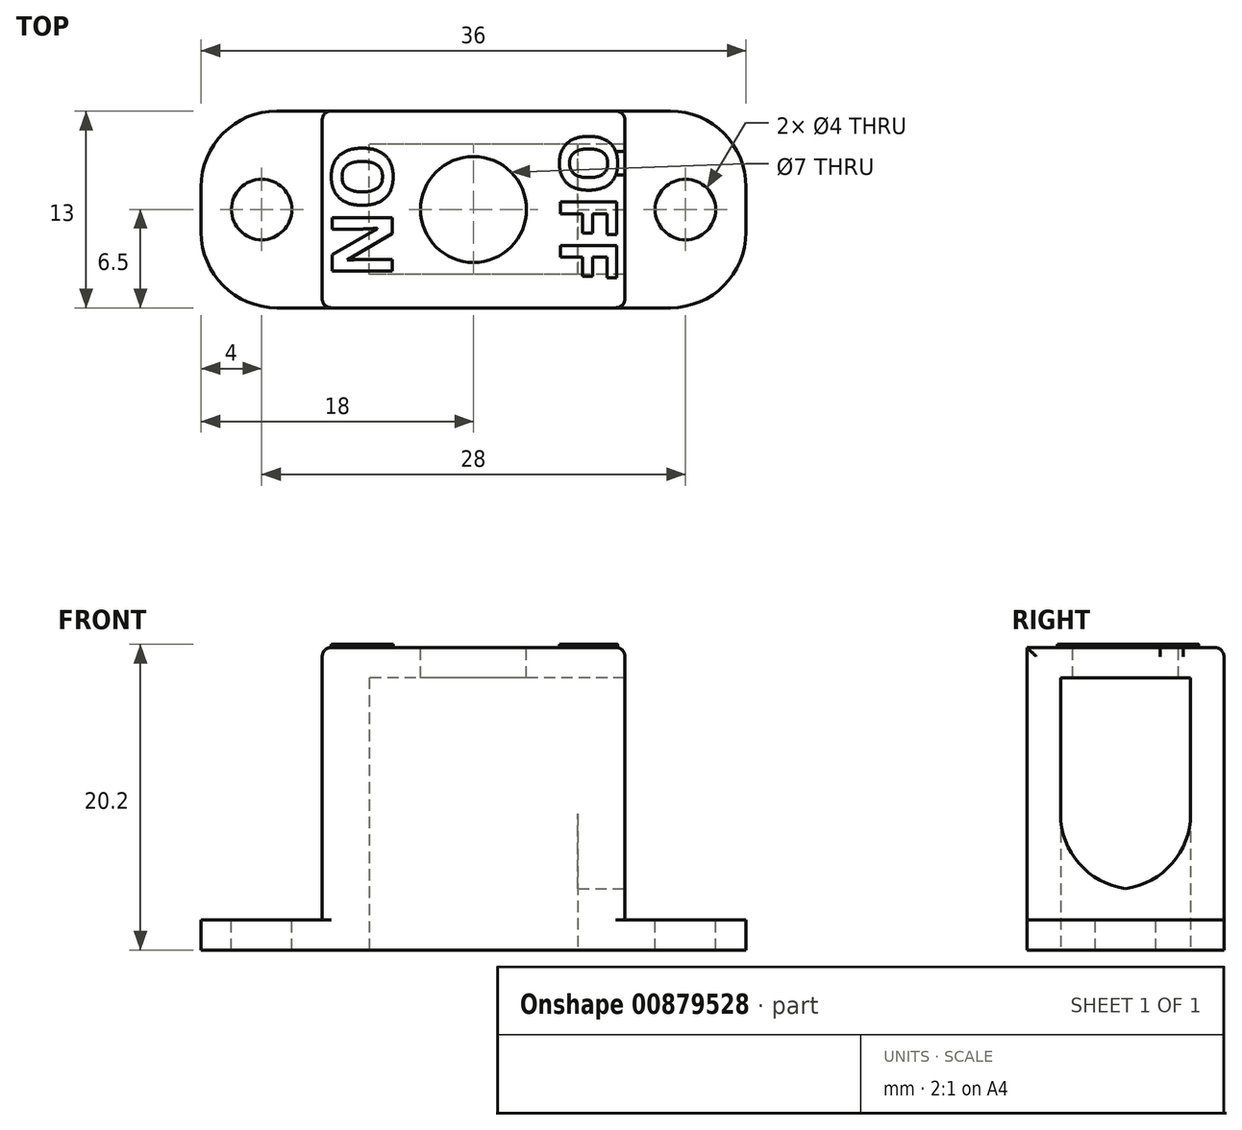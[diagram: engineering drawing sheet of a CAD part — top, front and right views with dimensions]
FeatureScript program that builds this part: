
annotation { "Feature Type Name" : "Feature", "Feature Type Description" : "" }
export const myFeature = defineFeature(function(context is Context, id is Id, definition is map)
    precondition{}
    {
        {
            var Q0;
            Q0=qCreatedBy(makeId("Top.planeOp"),FACE);
            var sketch = newSketch(context, id + "F0", { "sketchPlane" : qUnion([Q0])});
            skLineSegment(sketch, "E0.bottom", {"start": v(10, -6.5) * mm, "end": v(-10, -6.5) * mm});
            skLineSegment(sketch, "E0.top", {"start": v(10, 6.5) * mm, "end": v(-10, 6.5) * mm});
            skLineSegment(sketch, "E0.left", {"start": v(10, -6.5) * mm, "end": v(10, 6.5) * mm});
            skLineSegment(sketch, "E0.right", {"start": v(-10, -6.5) * mm, "end": v(-10, 6.5) * mm});
            skPoint(sketch, "E0.middle", {"position": v(0, 0) * mm});
            skLineSegment(sketch, "E1.bottom", {"start": v(6.9, -4.3) * mm, "end": v(-6.9, -4.3) * mm});
            skLineSegment(sketch, "E1.top", {"start": v(6.9, 4.3) * mm, "end": v(-6.9, 4.3) * mm});
            skLineSegment(sketch, "E1.left", {"start": v(6.9, -4.3) * mm, "end": v(6.9, 4.3) * mm});
            skLineSegment(sketch, "E1.right", {"start": v(-6.9, -4.3) * mm, "end": v(-6.9, 4.3) * mm});
            skSolve(sketch);
        }
        {
            var Q0;
            Q0=makeQuery(id+"F0.imprint","IMPRINT",FACE,{"disambiguationData":[TD([[makeQuery(id+"F0.imprint","IMPRINT",EDGE,{"derivedFrom":sQuery(id+"F0.wireOp",EDGE,"E0.bottom")}),-1.0]])]});
            extrude(context, id + "F1", {"entities" : qUnion([Q0]), "depth" : 16 * mm, "offsetDistance" : 25 * mm});
        }
        {
            var Q0;
            Q0=makeQuery(id+"F1.opExtrude","CAP_FACE",FACE,{"disambiguationData":[OSD([sQuery(id+"F0.wireOp",EDGE,"E0.bottom"),sQuery(id+"F0.wireOp",EDGE,"E0.top"),sQuery(id+"F0.wireOp",EDGE,"E0.left"),sQuery(id+"F0.wireOp",EDGE,"E0.right"),sQuery(id+"F0.wireOp",EDGE,"E1.bottom"),sQuery(id+"F0.wireOp",EDGE,"E1.top"),sQuery(id+"F0.wireOp",EDGE,"E1.left"),sQuery(id+"F0.wireOp",EDGE,"E1.right")])],"isStart":true});
            var sketch = newSketch(context, id + "F2", { "sketchPlane" : qUnion([Q0])});
            skLineSegment(sketch, "E2.bottom", {"start": v(18, -6.5) * mm, "end": v(-18, -6.5) * mm});
            skLineSegment(sketch, "E2.top", {"start": v(18, 6.5) * mm, "end": v(-18, 6.5) * mm});
            skLineSegment(sketch, "E2.left", {"start": v(18, -6.5) * mm, "end": v(18, 6.5) * mm});
            skLineSegment(sketch, "E2.right", {"start": v(-18, -6.5) * mm, "end": v(-18, 6.5) * mm});
            skPoint(sketch, "E2.middle", {"position": v(0, 0) * mm});
            skSolve(sketch);
        }
        {
            var Q0;
            Q0 = qSketchRegion(id + "F2", true);
            extrude(context, id + "F3", {"entities" : qUnion([Q0]), "operationType" : NewBodyOperationType.ADD, "depth" : 2 * mm, "offsetDistance" : 25 * mm});
        }
        {
            var Q0;
            Q0=makeQuery(id+"F1.opExtrude","CAP_FACE",FACE,{"disambiguationData":[OSD([sQuery(id+"F0.wireOp",EDGE,"E0.bottom"),sQuery(id+"F0.wireOp",EDGE,"E0.top"),sQuery(id+"F0.wireOp",EDGE,"E0.left"),sQuery(id+"F0.wireOp",EDGE,"E0.right"),sQuery(id+"F0.wireOp",EDGE,"E1.bottom"),sQuery(id+"F0.wireOp",EDGE,"E1.top"),sQuery(id+"F0.wireOp",EDGE,"E1.left"),sQuery(id+"F0.wireOp",EDGE,"E1.right")])],"isStart":false});
            var sketch = newSketch(context, id + "F4", { "sketchPlane" : qUnion([Q0])});
            skLineSegment(sketch, "E3.bottom", {"start": v(-10, 6.5) * mm, "end": v(10, 6.5) * mm});
            skLineSegment(sketch, "E3.top", {"start": v(-10, -6.5) * mm, "end": v(10, -6.5) * mm});
            skLineSegment(sketch, "E3.left", {"start": v(-10, 6.5) * mm, "end": v(-10, -6.5) * mm});
            skLineSegment(sketch, "E3.right", {"start": v(10, 6.5) * mm, "end": v(10, -6.5) * mm});
            skSolve(sketch);
        }
        {
            var Q0;
            Q0=makeQuery(id+"F1.opExtrude","CAP_EDGE",EDGE,{"disambiguationData":[OSD([sQuery(id+"F0.wireOp",EDGE,"E1.left")])],"isStart":true});
            var Q1;
            Q1=makeQuery(id+"F1.opExtrude","CAP_EDGE",EDGE,{"disambiguationData":[OSD([sQuery(id+"F0.wireOp",EDGE,"E1.left")])],"isStart":false});
            cPlane(context, id + "F5", {"entities" : qUnion([Q0, Q1]), "cplaneType" : CPlaneType.LINE_ANGLE, "offset" : 25 * mm, "angle" : 0 * degree, "width" : 150 * mm, "height" : 150 * mm});
        }
        {
            var Q0;
            Q0=qCreatedBy(id+"F5.planeOp",FACE);
            var sketch = newSketch(context, id + "F6", { "sketchPlane" : qUnion([Q0])});
            skLineSegment(sketch, "E4.bottom", {"start": v(-4.3, 2) * mm, "end": v(4.3, 2) * mm});
            skLineSegment(sketch, "E4.top", {"start": v(-4.3, 16) * mm, "end": v(4.3, 16) * mm});
            skLineSegment(sketch, "E4.left", {"start": v(-4.3, 2) * mm, "end": v(-4.3, 16) * mm});
            skLineSegment(sketch, "E4.right", {"start": v(4.3, 2) * mm, "end": v(4.3, 16) * mm});
            skPoint(sketch, "E5", {"position": v(-4.3, 2) * mm});
            skPoint(sketch, "E6", {"position": v(-4.3, 0) * mm});
            skSolve(sketch);
        }
        {
            var Q0;
            Q0 = qSketchRegion(id + "F6", true);
            var Q1;
            Q1=makeQuery(id+"F1.opExtrude","SWEPT_FACE",FACE,{"disambiguationData":[OSD([sQuery(id+"F0.wireOp",EDGE,"E0.left")])]});
            extrude(context, id + "F7", {"entities" : qUnion([Q0]), "operationType" : NewBodyOperationType.REMOVE, "endBound" : BoundingType.UP_TO_SURFACE, "depth" : 25 * mm, "endBoundEntityFace" : qUnion([Q1]), "offsetDistance" : 25 * mm});
        }
        {
            var Q0;
            Q0=makeQuery(id+"F4.imprint","IMPRINT",FACE,{"disambiguationData":[TD([[makeQuery(id+"F4.imprint","IMPRINT",EDGE,{"derivedFrom":sQuery(id+"F4.wireOp",EDGE,"E3.bottom")}),1.0]])]});
            var sketch = newSketch(context, id + "F8", { "sketchPlane" : qUnion([Q0])});
            skLineSegment(sketch, "E7.bottom", {"start": v(-10, 6.5) * mm, "end": v(10, 6.5) * mm});
            skLineSegment(sketch, "E7.top", {"start": v(-10, -6.5) * mm, "end": v(10, -6.5) * mm});
            skLineSegment(sketch, "E7.left", {"start": v(-10, 6.5) * mm, "end": v(-10, -6.5) * mm});
            skLineSegment(sketch, "E7.right", {"start": v(10, 6.5) * mm, "end": v(10, -6.5) * mm});
            skSolve(sketch);
        }
        {
            var Q0;
            Q0 = qSketchRegion(id + "F8", true);
            extrude(context, id + "F9", {"entities" : qUnion([Q0]), "operationType" : NewBodyOperationType.ADD, "depth" : 2 * mm, "offsetDistance" : 25 * mm});
        }
        {
            var Q0;
            Q0=makeQuery(id+"F9.opExtrude","CAP_FACE",FACE,{"disambiguationData":[OSD([sQuery(id+"F8.wireOp",EDGE,"E7.bottom"),sQuery(id+"F8.wireOp",EDGE,"E7.top"),sQuery(id+"F8.wireOp",EDGE,"E7.left"),sQuery(id+"F8.wireOp",EDGE,"E7.right")])],"isStart":false});
            var sketch = newSketch(context, id + "F10", { "sketchPlane" : qUnion([Q0])});
            skPoint(sketch, "E8", {"position": v(0, 0) * mm});
            skCircle(sketch, "E9", {"center": v(0, 0) * mm, "radius": 3.5 * mm});
            skSolve(sketch);
        }
        {
            var Q0;
            Q0 = qSketchRegion(id + "F10", true);
            var Q1;
            Q1=makeQuery(id+"F9.opExtrude","CAP_FACE",FACE,{"disambiguationData":[OSD([sQuery(id+"F8.wireOp",EDGE,"E7.bottom"),sQuery(id+"F8.wireOp",EDGE,"E7.top"),sQuery(id+"F8.wireOp",EDGE,"E7.left"),sQuery(id+"F8.wireOp",EDGE,"E7.right")])],"isStart":true});
            extrude(context, id + "F11", {"entities" : qUnion([Q0]), "operationType" : NewBodyOperationType.REMOVE, "endBound" : BoundingType.UP_TO_SURFACE, "oppositeDirection" : true, "depth" : 25 * mm, "endBoundEntityFace" : qUnion([Q1]), "offsetDistance" : 25 * mm});
        }
        {
            var Q0;
            {var subQ0=sQuery(id+"F2.wireOp",EDGE,"E2.top");var subQ1=sQuery(id+"F2.wireOp",EDGE,"E2.bottom");var subQ2=sQuery(id+"F2.wireOp",EDGE,"E2.left");Q0=makeQuery(id+"F3.boolean.opBoolean","SPLIT",FACE,{"disambiguationData":[TD([makeQuery(id+"F1.opExtrude","SWEPT_FACE",FACE,{"disambiguationData":[OSD([sQuery(id+"F0.wireOp",EDGE,"E0.left")])]})])],"derivedFrom":makeQuery(id+"F3.opExtrude","CAP_FACE",FACE,{"disambiguationData":[OSD([subQ1,subQ0,subQ2,sQuery(id+"F2.wireOp",EDGE,"E2.right")])],"isStart":true})});}
            var sketch = newSketch(context, id + "F12", { "sketchPlane" : qUnion([Q0])});
            skPoint(sketch, "E10", {"position": v(14, 0) * mm});
            skPoint(sketch, "E10.positionSnap0", {"position": v(14, 6.5) * mm});
            skPoint(sketch, "E10.positionSnap1", {"position": v(18, 0) * mm});
            skPoint(sketch, "E11", {"position": v(-14, 0) * mm});
            skPoint(sketch, "E12", {"position": v(-14, 6.5) * mm});
            skCircle(sketch, "E13", {"center": v(14, 0) * mm, "radius": 2 * mm});
            skCircle(sketch, "E14", {"center": v(-14, 0) * mm, "radius": 2 * mm});
            skSolve(sketch);
        }
        {
            var Q0;
            Q0=makeQuery(id+"F12.imprint","IMPRINT",FACE,{"disambiguationData":[TD([[makeQuery(id+"F12.imprint","IMPRINT",EDGE,{"derivedFrom":sQuery(id+"F12.wireOp",EDGE,"E13")}),1.0]])]});
            var Q1;
            Q1=makeQuery(id+"F12.imprint","IMPRINT",FACE,{"disambiguationData":[TD([[makeQuery(id+"F12.imprint","IMPRINT",EDGE,{"derivedFrom":sQuery(id+"F12.wireOp",EDGE,"E14")}),1.0]])]});
            var Q2;
            Q2=makeQuery(id+"F3.opExtrude","CAP_FACE",FACE,{"disambiguationData":[OSD([sQuery(id+"F2.wireOp",EDGE,"E2.bottom"),sQuery(id+"F2.wireOp",EDGE,"E2.top"),sQuery(id+"F2.wireOp",EDGE,"E2.left"),sQuery(id+"F2.wireOp",EDGE,"E2.right")])],"isStart":false});
            extrude(context, id + "F13", {"entities" : qUnion([Q0, Q1]), "operationType" : NewBodyOperationType.REMOVE, "endBound" : BoundingType.UP_TO_SURFACE, "oppositeDirection" : true, "depth" : 25 * mm, "endBoundEntityFace" : qUnion([Q2]), "offsetDistance" : 25 * mm});
        }
        {
            var Q0;
            Q0=makeQuery(id+"F9.opExtrude","CAP_FACE",FACE,{"disambiguationData":[OSD([sQuery(id+"F8.wireOp",EDGE,"E7.bottom"),sQuery(id+"F8.wireOp",EDGE,"E7.top"),sQuery(id+"F8.wireOp",EDGE,"E7.left"),sQuery(id+"F8.wireOp",EDGE,"E7.right")])],"isStart":false});
            var sketch = newSketch(context, id + "F14", { "sketchPlane" : qUnion([Q0])});
            skText(sketch, "E15", { "text": "ON", "fontName": "OpenSans-Bold.ttf"});
            skText(sketch, "E16", { "text": "OFF\n", "fontName": "OpenSans-Bold.ttf"});
            skLineSegment(sketch, "E17.bottom", {"start": v(18, 6.5) * mm, "end": v(-18, 6.5) * mm, "construction": true});
            skLineSegment(sketch, "E17.top", {"start": v(18, -6.5) * mm, "end": v(-18, -6.5) * mm, "construction": true});
            skLineSegment(sketch, "E17.left", {"start": v(18, 6.5) * mm, "end": v(18, -6.5) * mm, "construction": true});
            skLineSegment(sketch, "E17.right", {"start": v(-18, 6.5) * mm, "end": v(-18, -6.5) * mm, "construction": true});
            const initialGuessF14  = {"E15": [-0.00934, 0.00438, 0, -1, 0.004], "E16": [0.00573, 0.00514, 0, -1, 0.00377]};
            skSetInitialGuess(sketch, initialGuessF14);
            skSolve(sketch);
        }
        {
            var Q0;
            Q0 = qSketchRegion(id + "F14", true);
            extrude(context, id + "F15", {"entities" : qUnion([Q0]), "operationType" : NewBodyOperationType.ADD, "depth" : 0.2 * mm, "offsetDistance" : 25 * mm});
        }
        {
            var Q0;
            Q0=makeQuery(id+"F9.boolean.opBoolean","MERGE",EDGE,{"derivedFrom":[makeQuery(id+"F1.opExtrude","SWEPT_EDGE",EDGE,{"disambiguationData":[OSD([sQuery(id+"F0.wireOp",EDGE,"E0.bottom"),sQuery(id+"F0.wireOp",EDGE,"E0.left")])]}),makeQuery(id+"F9.opExtrude","SWEPT_EDGE",EDGE,{"disambiguationData":[OSD([sQuery(id+"F8.wireOp",EDGE,"E7.top"),sQuery(id+"F8.wireOp",EDGE,"E7.right")])]})]});
            var Q1;
            Q1=makeQuery(id+"F9.boolean.opBoolean","MERGE",EDGE,{"derivedFrom":[makeQuery(id+"F1.opExtrude","SWEPT_EDGE",EDGE,{"disambiguationData":[OSD([sQuery(id+"F0.wireOp",EDGE,"E0.bottom"),sQuery(id+"F0.wireOp",EDGE,"E0.right")])]}),makeQuery(id+"F9.opExtrude","SWEPT_EDGE",EDGE,{"disambiguationData":[OSD([sQuery(id+"F8.wireOp",EDGE,"E7.top"),sQuery(id+"F8.wireOp",EDGE,"E7.left")])]})]});
            var Q2;
            Q2=makeQuery(id+"F9.boolean.opBoolean","MERGE",EDGE,{"derivedFrom":[makeQuery(id+"F1.opExtrude","SWEPT_EDGE",EDGE,{"disambiguationData":[OSD([sQuery(id+"F0.wireOp",EDGE,"E0.top"),sQuery(id+"F0.wireOp",EDGE,"E0.left")])]}),makeQuery(id+"F9.opExtrude","SWEPT_EDGE",EDGE,{"disambiguationData":[OSD([sQuery(id+"F8.wireOp",EDGE,"E7.bottom"),sQuery(id+"F8.wireOp",EDGE,"E7.right")])]})]});
            var Q3;
            Q3=makeQuery(id+"F9.boolean.opBoolean","MERGE",EDGE,{"derivedFrom":[makeQuery(id+"F1.opExtrude","SWEPT_EDGE",EDGE,{"disambiguationData":[OSD([sQuery(id+"F0.wireOp",EDGE,"E0.top"),sQuery(id+"F0.wireOp",EDGE,"E0.right")])]}),makeQuery(id+"F9.opExtrude","SWEPT_EDGE",EDGE,{"disambiguationData":[OSD([sQuery(id+"F8.wireOp",EDGE,"E7.bottom"),sQuery(id+"F8.wireOp",EDGE,"E7.left")])]})]});
            var Q4;
            Q4=makeQuery(id+"F9.opExtrude","CAP_EDGE",EDGE,{"disambiguationData":[OSD([sQuery(id+"F8.wireOp",EDGE,"E7.bottom")])],"isStart":false});
            var Q5;
            Q5=makeQuery(id+"F9.opExtrude","CAP_EDGE",EDGE,{"disambiguationData":[OSD([sQuery(id+"F8.wireOp",EDGE,"E7.right")])],"isStart":false});
            var Q6;
            Q6=makeQuery(id+"F9.opExtrude","CAP_EDGE",EDGE,{"disambiguationData":[OSD([sQuery(id+"F8.wireOp",EDGE,"E7.left")])],"isStart":false});
            fillet(context, id + "F16", {"entities" : qUnion([Q0, Q1, Q2, Q3, Q4, Q5, Q6]), "radius" : 0.6 * mm, "tangentPropagation" : true, "allowEdgeOverflow" : false});
        }
        {
            var Q0;
            Q0=makeQuery(id+"F3.opExtrude","SWEPT_EDGE",EDGE,{"disambiguationData":[OSD([sQuery(id+"F2.wireOp",EDGE,"E2.bottom"),sQuery(id+"F2.wireOp",EDGE,"E2.right")])]});
            var Q1;
            Q1=makeQuery(id+"F3.opExtrude","SWEPT_EDGE",EDGE,{"disambiguationData":[OSD([sQuery(id+"F2.wireOp",EDGE,"E2.top"),sQuery(id+"F2.wireOp",EDGE,"E2.right")])]});
            var Q2;
            Q2=makeQuery(id+"F3.opExtrude","SWEPT_EDGE",EDGE,{"disambiguationData":[OSD([sQuery(id+"F2.wireOp",EDGE,"E2.bottom"),sQuery(id+"F2.wireOp",EDGE,"E2.left")])]});
            var Q3;
            Q3=makeQuery(id+"F3.opExtrude","SWEPT_EDGE",EDGE,{"disambiguationData":[OSD([sQuery(id+"F2.wireOp",EDGE,"E2.top"),sQuery(id+"F2.wireOp",EDGE,"E2.left")])]});
            var Q4;
            Q4=makeQuery(id+"F7.boolean.opBoolean","COPY",EDGE,{"derivedFrom":makeQuery(id+"F7.opExtrude","SWEPT_EDGE",EDGE,{"disambiguationData":[OSD([sQuery(id+"F6.wireOp",EDGE,"E4.bottom"),sQuery(id+"F6.wireOp",EDGE,"E4.right")])]})});
            var Q5;
            Q5=makeQuery(id+"F7.boolean.opBoolean","COPY",EDGE,{"derivedFrom":makeQuery(id+"F7.opExtrude","SWEPT_EDGE",EDGE,{"disambiguationData":[OSD([sQuery(id+"F6.wireOp",EDGE,"E4.bottom"),sQuery(id+"F6.wireOp",EDGE,"E4.left")])]})});
            fillet(context, id + "F17", {"entities" : qUnion([Q0, Q1, Q2, Q3, Q4, Q5]), "radius" : 5 * mm, "tangentPropagation" : true, "allowEdgeOverflow" : false});
        }
        {
            var Q0;
            Q0=makeQuery(id+"F3.boolean.opBoolean","SPLIT",FACE,{"disambiguationData":[TD([makeQuery(id+"F1.opExtrude","SWEPT_FACE",FACE,{"disambiguationData":[OSD([sQuery(id+"F0.wireOp",EDGE,"E1.bottom")])]})])],"derivedFrom":makeQuery(id+"F3.opExtrude","CAP_FACE",FACE,{"disambiguationData":[OSD([sQuery(id+"F2.wireOp",EDGE,"E2.bottom"),sQuery(id+"F2.wireOp",EDGE,"E2.top"),sQuery(id+"F2.wireOp",EDGE,"E2.left"),sQuery(id+"F2.wireOp",EDGE,"E2.right")])],"isStart":true})});
            var sketch = newSketch(context, id + "F18", { "sketchPlane" : qUnion([Q0])});
            skLineSegment(sketch, "E18.bottom", {"start": v(-6.9, -4.3) * mm, "end": v(6.9, -4.3) * mm});
            skLineSegment(sketch, "E18.top", {"start": v(-6.9, 4.3) * mm, "end": v(6.9, 4.3) * mm});
            skLineSegment(sketch, "E18.left", {"start": v(-6.9, -4.3) * mm, "end": v(-6.9, 4.3) * mm});
            skLineSegment(sketch, "E18.right", {"start": v(6.9, -4.3) * mm, "end": v(6.9, 4.3) * mm});
            skSolve(sketch);
        }
        {
            var Q0;
            Q0 = qSketchRegion(id + "F18", true);
            var Q1;
            Q1=makeQuery(id+"F3.opExtrude","CAP_FACE",FACE,{"disambiguationData":[OSD([sQuery(id+"F2.wireOp",EDGE,"E2.bottom"),sQuery(id+"F2.wireOp",EDGE,"E2.top"),sQuery(id+"F2.wireOp",EDGE,"E2.left"),sQuery(id+"F2.wireOp",EDGE,"E2.right")])],"isStart":false});
            extrude(context, id + "F19", {"entities" : qUnion([Q0]), "operationType" : NewBodyOperationType.REMOVE, "endBound" : BoundingType.UP_TO_SURFACE, "oppositeDirection" : true, "depth" : 25 * mm, "endBoundEntityFace" : qUnion([Q1]), "offsetDistance" : 25 * mm});
        }
    });
